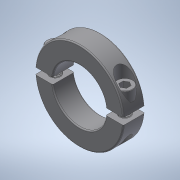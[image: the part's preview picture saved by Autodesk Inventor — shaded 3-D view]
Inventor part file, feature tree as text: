
AUTODESK INVENTOR PART (.ipt)
format: ipt  version: 2022.3 (Build 263350000, 350)  size: 1,282,048 bytes
history: native  units: mm (DEFAULTED — no unit token found)
features: mirror x2, other x2
ambient origin geometry x8: Origin, YZ Plane, XZ Plane, XY Plane, X Axis, Y Axis, Z Axis, Center Point
bodies: Solid1 (feature_tree), Solid2 (feature_tree), Solid3 (feature_tree), Solid4 (feature_tree)
feature tree (4):
  mirror  "Mirror1[1]"
  mirror  "Mirror1[2]"
  other  "Cut-Sweep1"
  other  "LPattern1"
